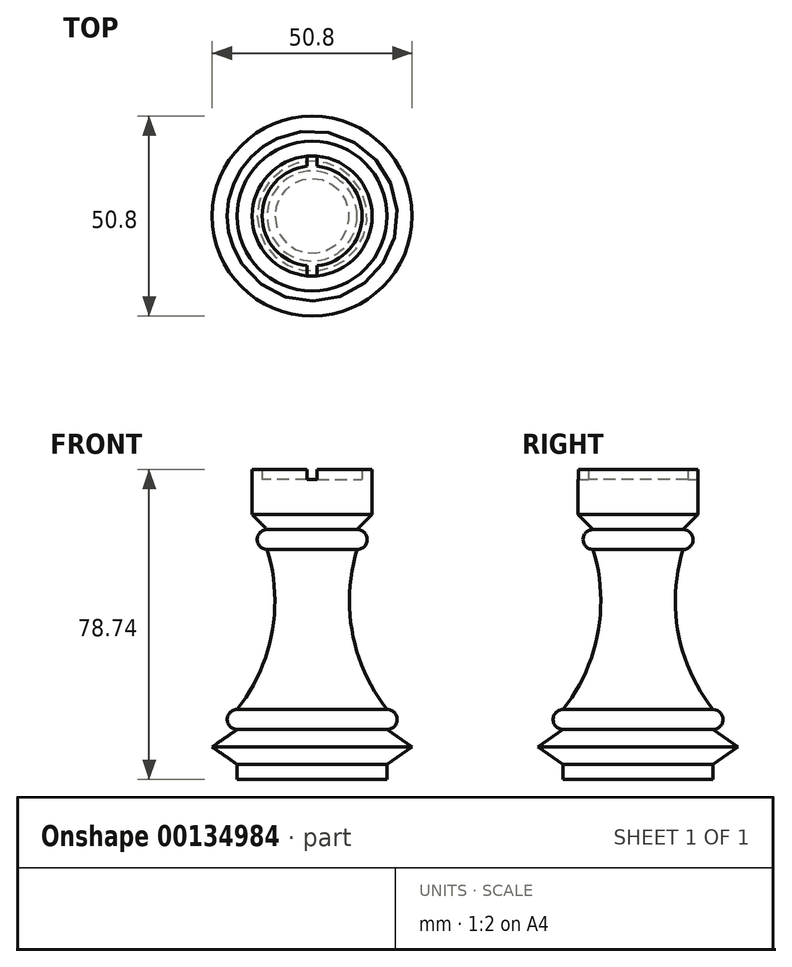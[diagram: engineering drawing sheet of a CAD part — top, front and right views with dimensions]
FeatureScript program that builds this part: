
annotation { "Feature Type Name" : "Feature", "Feature Type Description" : "" }
export const myFeature = defineFeature(function(context is Context, id is Id, definition is map)
    precondition{}
    {
        {
            var Q0;
            Q0=qCreatedBy(makeId("Front.planeOp"),FACE);
            var sketch = newSketch(context, id + "F0", { "sketchPlane" : qUnion([Q0])});
            skLineSegment(sketch, "E0", {"start": v(0, 0) * mm, "end": v(19.05, 0) * mm});
            skLineSegment(sketch, "E1", {"start": v(19.05, 3.81) * mm, "end": v(25.4, 8.26) * mm});
            skLineSegment(sketch, "E2", {"start": v(25.4, 8.26) * mm, "end": v(19.05, 12.7) * mm});
            skLineSegment(sketch, "E3", {"start": v(19.05, 3.81) * mm, "end": v(19.05, 0) * mm});
            skLineSegment(sketch, "E4", {"start": v(0, 0) * mm, "end": v(0, 76.2) * mm});
            skLineSegment(sketch, "E5", {"start": v(0, 76.2) * mm, "end": v(12.7, 76.2) * mm});
            skLineSegment(sketch, "E6", {"start": v(12.7, 76.2) * mm, "end": v(12.7, 78.74) * mm});
            skLineSegment(sketch, "E7", {"start": v(12.7, 78.74) * mm, "end": v(15.24, 78.74) * mm});
            skLineSegment(sketch, "E8", {"start": v(15.24, 78.74) * mm, "end": v(15.24, 67.31) * mm});
            skLineSegment(sketch, "E9", {"start": v(15.24, 67.31) * mm, "end": v(11.43, 63.5) * mm});
            skArc(sketch, "E10", {"start": v(11.43, 58.42) * mm, "mid": v(13.97, 60.96) * mm, "end": v(11.43, 63.5) * mm});
            skArc(sketch, "E11", {"start": v(19.05, 12.7) * mm, "mid": v(21.59, 15.24) * mm, "end": v(19.05, 17.78) * mm});
            skArc(sketch, "E12", {"start": v(11.43, 58.42) * mm, "mid": v(10.23, 37.16) * mm, "end": v(19.05, 17.78) * mm});
            skSolve(sketch);
        }
        {
            var Q0;
            Q0 = qSketchRegion(id + "F0", true);
            var Q1;
            Q1=sQuery(id+"F0.wireOp",EDGE,"E4");
            revolve(context, id + "F1", {"entities" : qUnion([Q0]), "axis" : qUnion([Q1]), "revolveType" : RevolveType.FULL});
        }
        {
            var Q0;
            Q0=qCreatedBy(makeId("Front.planeOp"),FACE);
            var sketch = newSketch(context, id + "F2", { "sketchPlane" : qUnion([Q0])});
            skLineSegment(sketch, "E13.bottom", {"start": v(-1.27, 76.2) * mm, "end": v(1.27, 76.2) * mm});
            skLineSegment(sketch, "E13.top", {"start": v(-1.27, 78.74) * mm, "end": v(1.27, 78.74) * mm});
            skLineSegment(sketch, "E13.left", {"start": v(-1.27, 76.2) * mm, "end": v(-1.27, 78.74) * mm});
            skLineSegment(sketch, "E13.right", {"start": v(1.27, 76.2) * mm, "end": v(1.27, 78.74) * mm});
            skPoint(sketch, "E13.middle", {"position": v(0, 77.47) * mm});
            skSolve(sketch);
        }
        {
            var Q0;
            Q0 = qSketchRegion(id + "F2", true);
            extrude(context, id + "F3", {"entities" : qUnion([Q0]), "operationType" : NewBodyOperationType.REMOVE, "endBound" : BoundingType.THROUGH_ALL, "depth" : 25.4 * mm, "hasSecondDirection" : true, "secondDirectionBound" : SecondDirectionBoundingType.THROUGH_ALL, "secondDirectionOppositeDirection" : true, "secondDirectionDepth" : 25.4 * mm});
        }
    });
